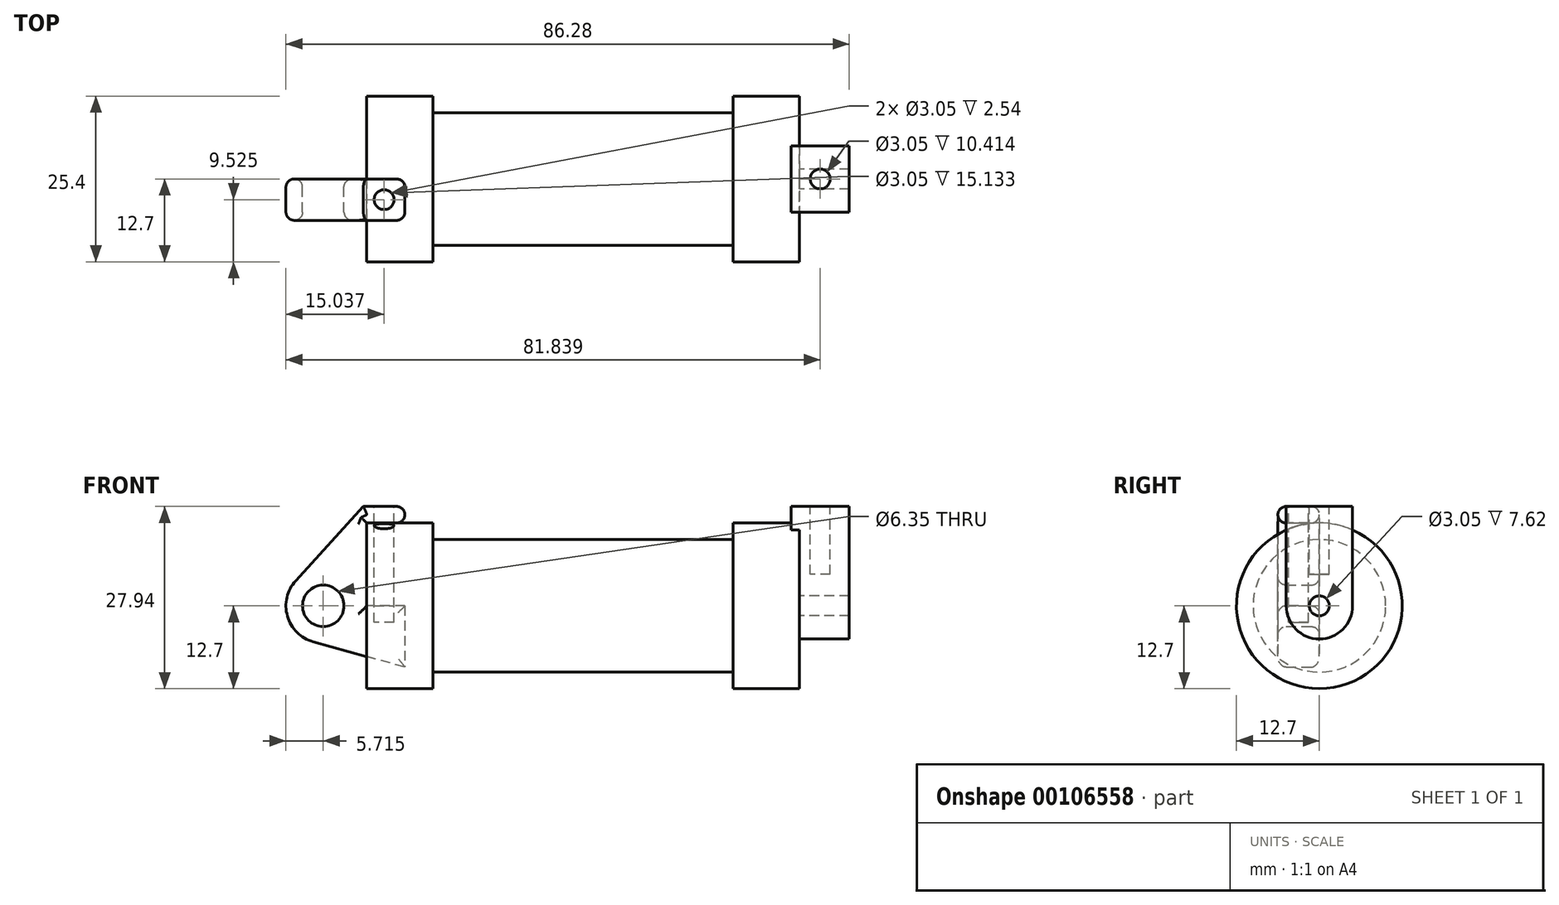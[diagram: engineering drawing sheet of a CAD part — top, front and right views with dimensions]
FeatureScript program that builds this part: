
annotation { "Feature Type Name" : "Feature", "Feature Type Description" : "" }
export const myFeature = defineFeature(function(context is Context, id is Id, definition is map)
    precondition{}
    {
        {
            var Q0;
            Q0=qCreatedBy(makeId("Front.planeOp"),FACE);
            var sketch = newSketch(context, id + "F0", { "sketchPlane" : qUnion([Q0])});
            skLineSegment(sketch, "E0", {"start": v(0, 0) * mm, "end": v(0, 12.7) * mm});
            skLineSegment(sketch, "E1", {"start": v(0, 12.7) * mm, "end": v(10.16, 12.7) * mm});
            skLineSegment(sketch, "E2", {"start": v(10.16, 12.7) * mm, "end": v(10.16, 10.16) * mm});
            skLineSegment(sketch, "E3", {"start": v(10.16, 10.16) * mm, "end": v(56.13, 10.16) * mm});
            skLineSegment(sketch, "E4", {"start": v(56.13, 10.16) * mm, "end": v(56.13, 12.7) * mm});
            skLineSegment(sketch, "E5", {"start": v(56.13, 12.7) * mm, "end": v(66.3, 12.7) * mm});
            skLineSegment(sketch, "E6", {"start": v(66.3, 12.7) * mm, "end": v(66.3, 0) * mm});
            skLineSegment(sketch, "E7", {"start": v(66.3, 0) * mm, "end": v(0, 0) * mm});
            skLineSegment(sketch, "E8", {"start": v(5.84, 15.24) * mm, "end": v(-0.5, 15.24) * mm});
            skLineSegment(sketch, "E9", {"start": v(-0.5, 15.24) * mm, "end": v(-10.88, 3.85) * mm});
            skLineSegment(sketch, "E10", {"start": v(0, 0) * mm, "end": v(-6.65, 0) * mm});
            skCircle(sketch, "E11", {"center": v(-6.65, 0) * mm, "radius": 5.72 * mm});
            skCircle(sketch, "E12", {"center": v(-6.65, 0) * mm, "radius": 3.18 * mm});
            skLineSegment(sketch, "E13", {"start": v(5.84, 15.24) * mm, "end": v(5.84, -9.4) * mm});
            skLineSegment(sketch, "E14", {"start": v(5.84, -9.4) * mm, "end": v(-8.18, -5.5) * mm});
            skSolve(sketch);
        }
        {
            var Q0;
            {var subQ0=sQuery(id+"F0.wireOp",EDGE,"E0");Q0=makeQuery(id+"F0.imprint","IMPRINT",FACE,{"disambiguationData":[TD([[makeQuery(id+"F0.imprint","IMPRINT",EDGE,{"derivedFrom":subQ0}),-1.0]])]});}
            var Q1;
            {var subQ0=sQuery(id+"F0.wireOp",EDGE,"E2");Q1=makeQuery(id+"F0.imprint","IMPRINT",FACE,{"disambiguationData":[TD([[makeQuery(id+"F0.imprint","IMPRINT",EDGE,{"derivedFrom":subQ0}),-1.0]])]});}
            var Q2;
            Q2=sQuery(id+"F0.wireOp",EDGE,"E7");
            revolve(context, id + "F1", {"entities" : qUnion([Q0, Q1]), "axis" : qUnion([Q2]), "revolveType" : RevolveType.FULL});
        }
        {
            var Q0;
            {var subQ3=sQuery(id+"F0.wireOp",EDGE,"E0");Q0=makeQuery(id+"F0.imprint","IMPRINT",FACE,{"disambiguationData":[TD([[makeQuery(id+"F0.imprint","IMPRINT",EDGE,{"derivedFrom":subQ3}),1.0]])]});}
            var Q1;
            {var subQ4=sQuery(id+"F0.wireOp",EDGE,"E12");Q1=makeQuery(id+"F0.imprint","IMPRINT",FACE,{"disambiguationData":[TD([[makeQuery(id+"F0.imprint","IMPRINT",EDGE,{"derivedFrom":subQ4}),-1.0]])]});}
            var Q2;
            {var subQ0=sQuery(id+"F0.wireOp",EDGE,"E14");Q2=makeQuery(id+"F0.imprint","IMPRINT",FACE,{"disambiguationData":[TD([[makeQuery(id+"F0.imprint","IMPRINT",EDGE,{"derivedFrom":subQ0}),-1.0]])]});}
            extrude(context, id + "F2", {"entities" : qUnion([Q0, Q1, Q2]), "depth" : 6.35 * mm});
        }
        {
            var Q0;
            Q0=makeQuery(id+"F1.opRevolve","SWEPT_FACE",FACE,{"disambiguationData":[OSD([sQuery(id+"F0.wireOp",EDGE,"E6")])]});
            var sketch = newSketch(context, id + "F3", { "sketchPlane" : qUnion([Q0])});
            skCircle(sketch, "E15", {"center": v(0, 0) * mm, "radius": 5.08 * mm});
            skCircle(sketch, "E16", {"center": v(0, 0) * mm, "radius": 1.52 * mm});
            skLineSegment(sketch, "E17", {"start": v(5.08, 0) * mm, "end": v(5.08, 15.24) * mm});
            skLineSegment(sketch, "E18", {"start": v(-5.08, 0) * mm, "end": v(-5.08, 15.24) * mm});
            skLineSegment(sketch, "E19", {"start": v(-5.08, 15.24) * mm, "end": v(5.08, 15.24) * mm});
            skSolve(sketch);
        }
        {
            var Q0;
            Q0 = qSketchRegion(id + "F3", true);
            extrude(context, id + "F4", {"entities" : qUnion([Q0]), "operationType" : NewBodyOperationType.ADD, "depth" : 7.62 * mm, "hasSecondDirection" : true, "secondDirectionOppositeDirection" : true, "secondDirectionDepth" : 1.27 * mm});
        }
        {
            var Q0;
            Q0=makeQuery(id+"F4.opExtrude","SWEPT_FACE",FACE,{"disambiguationData":[OSD([sQuery(id+"F3.wireOp",EDGE,"E19")])]});
            var sketch = newSketch(context, id + "F5", { "sketchPlane" : qUnion([Q0])});
            skCircle(sketch, "E20", {"center": v(69.47, 0) * mm, "radius": 1.52 * mm});
            skPoint(sketch, "E20.centerSnap0", {"position": v(69.47, 5.08) * mm});
            skPoint(sketch, "E20.centerSnap1", {"position": v(65.02, 0) * mm});
            skSolve(sketch);
        }
        {
            var Q0;
            Q0=makeQuery(id+"F5.imprint","IMPRINT",FACE,{"disambiguationData":[TD([[makeQuery(id+"F5.imprint","IMPRINT",EDGE,{"derivedFrom":sQuery(id+"F5.wireOp",EDGE,"E20")}),1.0]])]});
            extrude(context, id + "F6", {"entities" : qUnion([Q0]), "operationType" : NewBodyOperationType.REMOVE, "oppositeDirection" : true, "depth" : 10.4 * mm});
        }
        {
            var Q0;
            Q0=makeQuery(id+"F2.opExtrude","SWEPT_FACE",FACE,{"disambiguationData":[OSD([sQuery(id+"F0.wireOp",EDGE,"E8")])]});
            var sketch = newSketch(context, id + "F7", { "sketchPlane" : qUnion([Q0])});
            skCircle(sketch, "E21", {"center": v(2.67, -3.18) * mm, "radius": 1.52 * mm});
            skPoint(sketch, "E21.centerSnap0", {"position": v(-0.5, -3.18) * mm});
            skPoint(sketch, "E21.centerSnap1", {"position": v(2.67, 0) * mm});
            skSolve(sketch);
        }
        {
            var Q0;
            Q0=makeQuery(id+"F7.imprint","IMPRINT",FACE,{"disambiguationData":[TD([[makeQuery(id+"F7.imprint","IMPRINT",EDGE,{"derivedFrom":sQuery(id+"F7.wireOp",EDGE,"E21")}),1.0]])]});
            extrude(context, id + "F8", {"entities" : qUnion([Q0]), "operationType" : NewBodyOperationType.REMOVE, "oppositeDirection" : true, "depth" : 17.78 * mm});
        }
        {
            var Q0;
            Q0=makeQuery(id+"F4.opExtrude","CAP_EDGE",EDGE,{"disambiguationData":[OSD([sQuery(id+"F3.wireOp",EDGE,"E19")])],"isStart":true});
            var Q1;
            Q1=makeQuery(id+"F4.opExtrude","CAP_EDGE",EDGE,{"disambiguationData":[OSD([sQuery(id+"F3.wireOp",EDGE,"E19")])],"isStart":false});
            var Q2;
            Q2=makeQuery(id+"F1.opRevolve","SWEPT_EDGE",EDGE,{"disambiguationData":[OSD([sQuery(id+"F0.wireOp",EDGE,"E5"),sQuery(id+"F0.wireOp",EDGE,"E6")])]});
            var Q3;
            Q3=makeQuery(id+"F1.opRevolve","SWEPT_EDGE",EDGE,{"disambiguationData":[OSD([sQuery(id+"F0.wireOp",EDGE,"E4"),sQuery(id+"F0.wireOp",EDGE,"E5")])]});
            var Q4;
            Q4=makeQuery(id+"F1.opRevolve","SWEPT_EDGE",EDGE,{"disambiguationData":[OSD([sQuery(id+"F0.wireOp",EDGE,"E1"),sQuery(id+"F0.wireOp",EDGE,"E2")])]});
            var Q5;
            Q5=makeQuery(id+"F1.opRevolve","SWEPT_EDGE",EDGE,{"disambiguationData":[OSD([sQuery(id+"F0.wireOp",EDGE,"E0"),sQuery(id+"F0.wireOp",EDGE,"E1")])]});
            var Q6;
            Q6=makeQuery(id+"F2.opExtrude","CAP_EDGE",EDGE,{"disambiguationData":[OSD([sQuery(id+"F0.wireOp",EDGE,"E8")])],"isStart":false});
            var Q7;
            Q7=makeQuery(id+"F2.opExtrude","SWEPT_EDGE",EDGE,{"disambiguationData":[OSD([sQuery(id+"F0.wireOp",EDGE,"E8"),sQuery(id+"F0.wireOp",EDGE,"E13")])]});
            var Q8;
            Q8=makeQuery(id+"F2.opExtrude","CAP_EDGE",EDGE,{"disambiguationData":[OSD([sQuery(id+"F0.wireOp",EDGE,"E8")])],"isStart":true});
            var Q9;
            Q9=makeQuery(id+"F2.opExtrude","SWEPT_EDGE",EDGE,{"disambiguationData":[OSD([sQuery(id+"F0.wireOp",EDGE,"E1"),sQuery(id+"F0.wireOp",EDGE,"E13")])]});
            var Q10;
            Q10=makeQuery(id+"F2.opExtrude","CAP_EDGE",EDGE,{"disambiguationData":[OSD([sQuery(id+"F0.wireOp",EDGE,"E1")])],"isStart":false});
            var Q11;
            {var subQ0=sQuery(id+"F0.wireOp",EDGE,"E13");Q11=makeQuery(id+"F2.opExtrude","CAP_EDGE",EDGE,{"disambiguationData":[OSD([subQ0]),TDD([makeQuery(id+"F0.imprint","IMPRINT",EDGE,{"disambiguationData":[TD([[makeQuery(id+"F0.imprint","INTERSECT",VERTEX,{"derivedFrom":[sQuery(id+"F0.wireOp",EDGE,"E8"),subQ0]}),-1.0]])],"derivedFrom":subQ0})])],"isStart":false});}
            var Q12;
            {var subQ0=sQuery(id+"F0.wireOp",EDGE,"E13");Q12=makeQuery(id+"F2.opExtrude","CAP_EDGE",EDGE,{"disambiguationData":[OSD([subQ0]),TDD([makeQuery(id+"F0.imprint","IMPRINT",EDGE,{"disambiguationData":[TD([[makeQuery(id+"F0.imprint","INTERSECT",VERTEX,{"derivedFrom":[sQuery(id+"F0.wireOp",EDGE,"E8"),subQ0]}),-1.0]])],"derivedFrom":subQ0})])],"isStart":true});}
            var Q13;
            Q13=makeQuery(id+"F1.opRevolve","SWEPT_FACE",FACE,{"disambiguationData":[OSD([sQuery(id+"F0.wireOp",EDGE,"E3")])]});
            var Q14;
            Q14=makeQuery(id+"F2.opExtrude","CAP_FACE",FACE,{"disambiguationData":[OSD([sQuery(id+"F0.wireOp",EDGE,"E0"),sQuery(id+"F0.wireOp",EDGE,"E1"),sQuery(id+"F0.wireOp",EDGE,"E7"),sQuery(id+"F0.wireOp",EDGE,"E8"),sQuery(id+"F0.wireOp",EDGE,"E9"),sQuery(id+"F0.wireOp",EDGE,"E11"),sQuery(id+"F0.wireOp",EDGE,"E12"),sQuery(id+"F0.wireOp",EDGE,"E13"),sQuery(id+"F0.wireOp",EDGE,"E14")])],"isStart":false});
            var Q15;
            Q15=makeQuery(id+"F2.opExtrude","CAP_FACE",FACE,{"disambiguationData":[OSD([sQuery(id+"F0.wireOp",EDGE,"E0"),sQuery(id+"F0.wireOp",EDGE,"E1"),sQuery(id+"F0.wireOp",EDGE,"E7"),sQuery(id+"F0.wireOp",EDGE,"E8"),sQuery(id+"F0.wireOp",EDGE,"E9"),sQuery(id+"F0.wireOp",EDGE,"E11"),sQuery(id+"F0.wireOp",EDGE,"E12"),sQuery(id+"F0.wireOp",EDGE,"E13"),sQuery(id+"F0.wireOp",EDGE,"E14")])],"isStart":true});
            var Q16;
            Q16=makeQuery(id+"F1.opRevolve","SWEPT_EDGE",EDGE,{"disambiguationData":[OSD([sQuery(id+"F0.wireOp",EDGE,"E2"),sQuery(id+"F0.wireOp",EDGE,"E3")])]});
            var Q17;
            Q17=makeQuery(id+"F1.opRevolve","SWEPT_FACE",FACE,{"disambiguationData":[OSD([sQuery(id+"F0.wireOp",EDGE,"E4")])]});
            var Q18;
            Q18=makeQuery(id+"F4.opExtrude","CAP_FACE",FACE,{"disambiguationData":[OSD([sQuery(id+"F3.wireOp",EDGE,"E15"),sQuery(id+"F3.wireOp",EDGE,"E16"),sQuery(id+"F3.wireOp",EDGE,"E17"),sQuery(id+"F3.wireOp",EDGE,"E18"),sQuery(id+"F3.wireOp",EDGE,"E19")])],"isStart":false});
            var Q19;
            Q19=makeQuery(id+"F4.opExtrude","CAP_FACE",FACE,{"disambiguationData":[OSD([sQuery(id+"F3.wireOp",EDGE,"E15"),sQuery(id+"F3.wireOp",EDGE,"E16"),sQuery(id+"F3.wireOp",EDGE,"E17"),sQuery(id+"F3.wireOp",EDGE,"E18"),sQuery(id+"F3.wireOp",EDGE,"E19")])],"isStart":true});
            fillet(context, id + "F9", {"entities" : qUnion([Q0, Q1, Q2, Q3, Q4, Q5, Q6, Q7, Q8, Q9, Q10, Q11, Q12, Q13, Q14, Q15, Q16, Q17, Q18, Q19]), "radius" : 1.27 * mm, "tangentPropagation" : true, "allowEdgeOverflow" : false});
        }
    });
